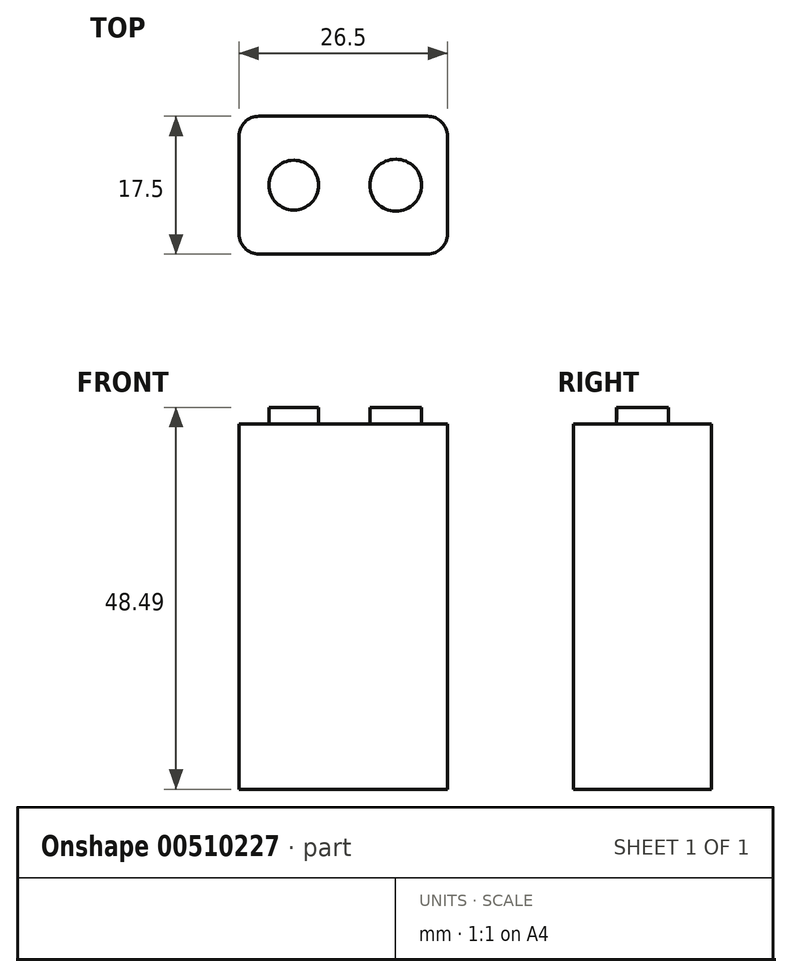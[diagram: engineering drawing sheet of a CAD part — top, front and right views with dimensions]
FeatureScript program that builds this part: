
annotation { "Feature Type Name" : "Feature", "Feature Type Description" : "" }
export const myFeature = defineFeature(function(context is Context, id is Id, definition is map)
    precondition{}
    {
        {
            var Q0;
            Q0=qCreatedBy(makeId("Top.planeOp"),FACE);
            var sketch = newSketch(context, id + "F0", { "sketchPlane" : qUnion([Q0])});
            skLineSegment(sketch, "E0.bottom", {"start": v(13.25, -8.75) * mm, "end": v(-13.25, -8.75) * mm});
            skLineSegment(sketch, "E0.top", {"start": v(13.25, 8.75) * mm, "end": v(-13.25, 8.75) * mm});
            skLineSegment(sketch, "E0.left", {"start": v(13.25, -8.75) * mm, "end": v(13.25, 8.75) * mm});
            skLineSegment(sketch, "E0.right", {"start": v(-13.25, -8.75) * mm, "end": v(-13.25, 8.75) * mm});
            skPoint(sketch, "E0.middle", {"position": v(0, 0) * mm});
            skSolve(sketch);
        }
        {
            var Q0;
            Q0 = qSketchRegion(id + "F0", true);
            extrude(context, id + "F1", {"entities" : qUnion([Q0]), "depth" : 46.4 * mm});
        }
        {
            var Q0;
            Q0=makeQuery(id+"F1.opExtrude","CAP_FACE",FACE,{"disambiguationData":[OSD([sQuery(id+"F0.wireOp",EDGE,"E0.bottom"),sQuery(id+"F0.wireOp",EDGE,"E0.top"),sQuery(id+"F0.wireOp",EDGE,"E0.left"),sQuery(id+"F0.wireOp",EDGE,"E0.right")])],"isStart":false});
            var sketch = newSketch(context, id + "F2", { "sketchPlane" : qUnion([Q0])});
            skCircle(sketch, "E1", {"center": v(-6.28, 0) * mm, "radius": 3.16 * mm});
            skCircle(sketch, "E2", {"center": v(6.67, 0) * mm, "radius": 3.3 * mm});
            skSolve(sketch);
        }
        {
            var Q0;
            Q0=makeQuery(id+"F2.imprint","IMPRINT",FACE,{"disambiguationData":[TD([[makeQuery(id+"F2.imprint","IMPRINT",EDGE,{"derivedFrom":sQuery(id+"F2.wireOp",EDGE,"E1")}),1.0]])]});
            var Q1;
            Q1=makeQuery(id+"F2.imprint","IMPRINT",FACE,{"disambiguationData":[TD([[makeQuery(id+"F2.imprint","IMPRINT",EDGE,{"derivedFrom":sQuery(id+"F2.wireOp",EDGE,"E2")}),1.0]])]});
            extrude(context, id + "F3", {"entities" : qUnion([Q0, Q1]), "operationType" : NewBodyOperationType.ADD, "depth" : 2.08 * mm});
        }
        {
            var Q0;
            Q0=makeQuery(id+"F1.opExtrude","SWEPT_EDGE",EDGE,{"disambiguationData":[OSD([sQuery(id+"F0.wireOp",EDGE,"E0.bottom"),sQuery(id+"F0.wireOp",EDGE,"E0.right")])]});
            var Q1;
            Q1=makeQuery(id+"F1.opExtrude","SWEPT_EDGE",EDGE,{"disambiguationData":[OSD([sQuery(id+"F0.wireOp",EDGE,"E0.bottom"),sQuery(id+"F0.wireOp",EDGE,"E0.left")])]});
            var Q2;
            Q2=makeQuery(id+"F1.opExtrude","SWEPT_EDGE",EDGE,{"disambiguationData":[OSD([sQuery(id+"F0.wireOp",EDGE,"E0.top"),sQuery(id+"F0.wireOp",EDGE,"E0.left")])]});
            var Q3;
            Q3=makeQuery(id+"F1.opExtrude","SWEPT_EDGE",EDGE,{"disambiguationData":[OSD([sQuery(id+"F0.wireOp",EDGE,"E0.top"),sQuery(id+"F0.wireOp",EDGE,"E0.right")])]});
            fillet(context, id + "F4", {"entities" : qUnion([Q0, Q1, Q2, Q3]), "radius" : 2.54 * mm, "tangentPropagation" : true, "allowEdgeOverflow" : false});
        }
    });
